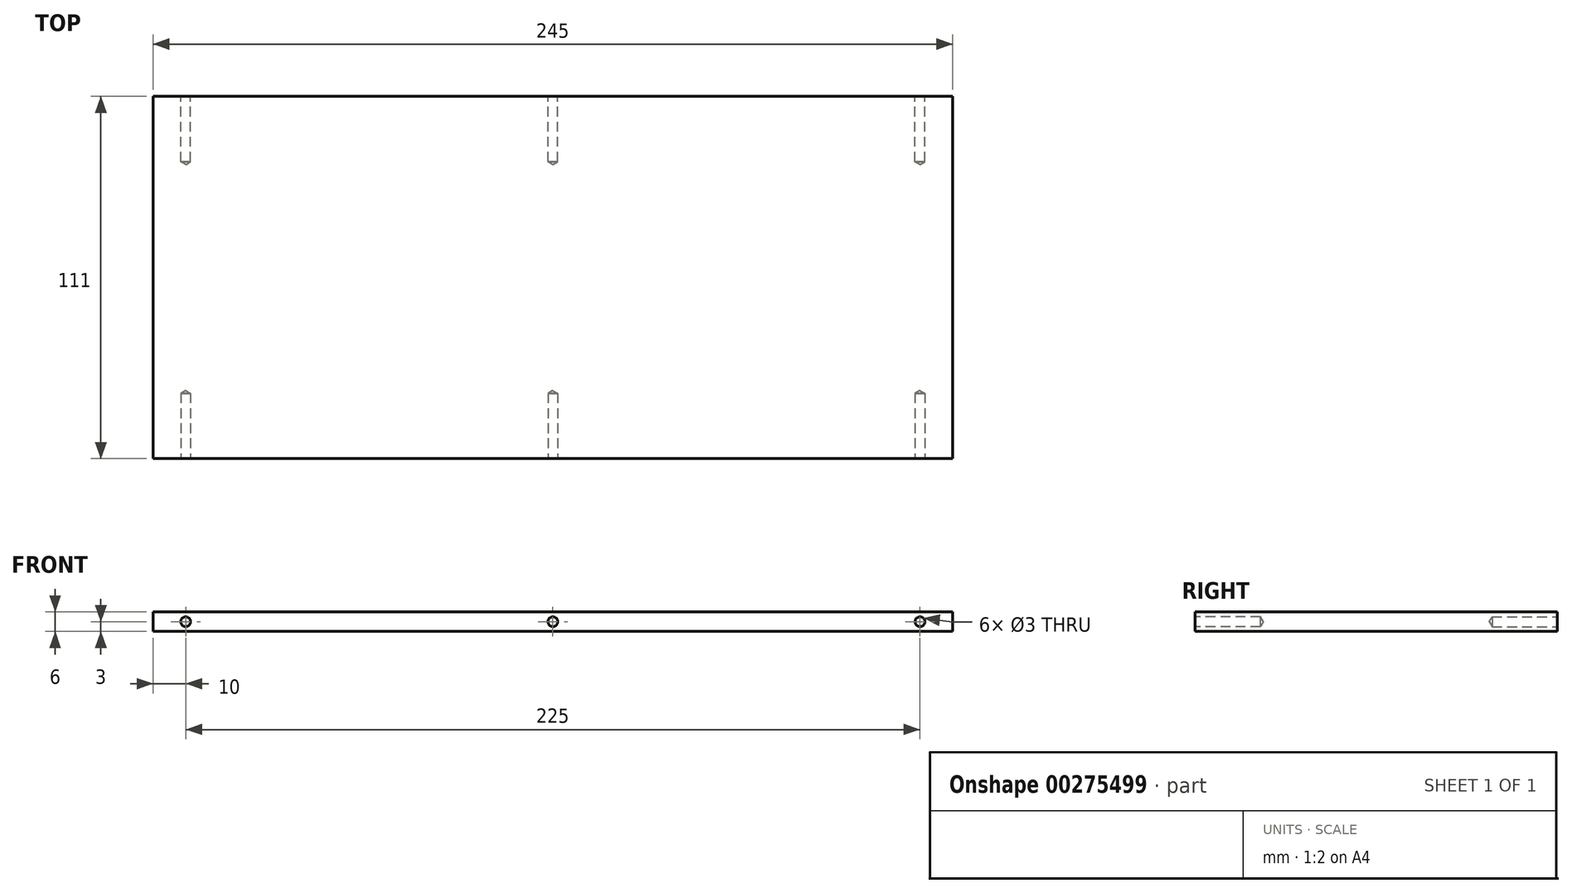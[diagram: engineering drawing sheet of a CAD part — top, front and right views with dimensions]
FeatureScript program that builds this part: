
annotation { "Feature Type Name" : "Feature", "Feature Type Description" : "" }
export const myFeature = defineFeature(function(context is Context, id is Id, definition is map)
    precondition{}
    {
        {
            var Q0;
            Q0=qCreatedBy(makeId("Top.planeOp"),FACE);
            var sketch = newSketch(context, id + "F0", { "sketchPlane" : qUnion([Q0])});
            skLineSegment(sketch, "E0.bottom", {"start": v(0, 0) * mm, "end": v(245, 0) * mm});
            skLineSegment(sketch, "E0.top", {"start": v(0, 111) * mm, "end": v(245, 111) * mm});
            skLineSegment(sketch, "E0.left", {"start": v(0, 0) * mm, "end": v(0, 111) * mm});
            skLineSegment(sketch, "E0.right", {"start": v(245, 0) * mm, "end": v(245, 111) * mm});
            skSolve(sketch);
        }
        {
            var Q0;
            Q0=makeQuery(id+"F0.imprint","IMPRINT",FACE,{"disambiguationData":[TD([[makeQuery(id+"F0.imprint","IMPRINT",EDGE,{"derivedFrom":sQuery(id+"F0.wireOp",EDGE,"E0.bottom")}),1.0]])]});
            extrude(context, id + "F1", {"entities" : qUnion([Q0]), "depth" : 6 * mm});
        }
        {
            var Q0;
            Q0=makeQuery(id+"F1.opExtrude","SWEPT_FACE",FACE,{"disambiguationData":[OSD([sQuery(id+"F0.wireOp",EDGE,"E0.bottom")])]});
            var sketch = newSketch(context, id + "F2", { "sketchPlane" : qUnion([Q0])});
            skPoint(sketch, "E1", {"position": v(10, 3) * mm});
            skPoint(sketch, "E1.positionSnap0", {"position": v(0, 3) * mm});
            skPoint(sketch, "E2", {"position": v(235, 3) * mm});
            skPoint(sketch, "E2.positionSnap0", {"position": v(245, 3) * mm});
            skPoint(sketch, "E3", {"position": v(122.5, 3) * mm});
            skSolve(sketch);
        }
        {
            var Q0;
            Q0=sQuery(id+"F2.wireOp",VERTEX,"E1");
            var Q1;
            Q1=sQuery(id+"F2.wireOp",VERTEX,"E3");
            var Q2;
            Q2=sQuery(id+"F2.wireOp",VERTEX,"E2");
            var Q3;
            Q3=makeQuery(id+"F1.opExtrude","SWEPT_BODY",BODY,{"disambiguationData":[OSD([sQuery(id+"F0.wireOp",EDGE,"E0.bottom"),sQuery(id+"F0.wireOp",EDGE,"E0.top"),sQuery(id+"F0.wireOp",EDGE,"E0.left"),sQuery(id+"F0.wireOp",EDGE,"E0.right")])]});
            hole(context, id + "F3", {"style" : HoleStyle.SIMPLE, "endStyle" : HoleEndStyle.BLIND, "holeDiameter" : 3 * mm, "holeDepth" : 20 * mm, "tappedDepth" : 12 * mm, "tapClearance" : 3, "locations" : qUnion([Q0, Q1, Q2]), "scope" : qUnion([Q3])});
        }
        {
            var Q0;
            Q0=makeQuery(id+"F1.opExtrude","SWEPT_FACE",FACE,{"disambiguationData":[OSD([sQuery(id+"F0.wireOp",EDGE,"E0.top")])]});
            var sketch = newSketch(context, id + "F4", { "sketchPlane" : qUnion([Q0])});
            skPoint(sketch, "E4", {"position": v(-235, 3) * mm});
            skPoint(sketch, "E4.positionSnap0", {"position": v(-245, 3) * mm});
            skPoint(sketch, "E5", {"position": v(-10, 3) * mm});
            skPoint(sketch, "E5.positionSnap0", {"position": v(0, 3) * mm});
            skPoint(sketch, "E6", {"position": v(-122.5, 3) * mm});
            skSolve(sketch);
        }
        {
            var Q0;
            Q0=sQuery(id+"F4.wireOp",VERTEX,"E4");
            var Q1;
            Q1=sQuery(id+"F4.wireOp",VERTEX,"E6");
            var Q2;
            Q2=sQuery(id+"F4.wireOp",VERTEX,"E5");
            var Q3;
            Q3=makeQuery(id+"F1.opExtrude","SWEPT_BODY",BODY,{"disambiguationData":[OSD([sQuery(id+"F0.wireOp",EDGE,"E0.bottom"),sQuery(id+"F0.wireOp",EDGE,"E0.top"),sQuery(id+"F0.wireOp",EDGE,"E0.left"),sQuery(id+"F0.wireOp",EDGE,"E0.right")])]});
            hole(context, id + "F5", {"style" : HoleStyle.SIMPLE, "endStyle" : HoleEndStyle.BLIND, "holeDiameter" : 3 * mm, "holeDepth" : 20 * mm, "tappedDepth" : 12 * mm, "tapClearance" : 3, "locations" : qUnion([Q0, Q1, Q2]), "scope" : qUnion([Q3])});
        }
    });
